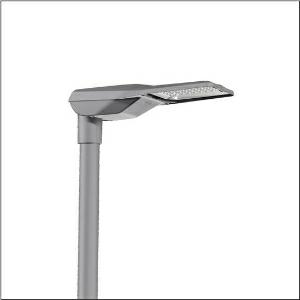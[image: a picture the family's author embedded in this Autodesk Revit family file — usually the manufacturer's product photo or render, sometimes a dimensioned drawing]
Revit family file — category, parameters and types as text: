
# Revit family: streetlight_sl_21_iq_mini___p1_0a_5xe2a31d08hb_09ea
name_source: partatom
category: Lighting Fixtures
units: mm (PartAtom-declared; Revit-internal decimal feet)

## family parameters
Cut with Voids When Loaded = No
Host = Face
Light Source = No
Part Type = Normal
Room Calculation Point = No
Round Connector Dimension = Use Diameter
Shared = No

## types (1)
- --- (1 x LED, 9450 lm, 70.9 W, 3000K)
    Apparent Load = 71 VA
    CIE Flux Codes = 21 50 90 100 100
    Color Rendering = 70
    Color Temperature = 3000K
    Default Elevation = 1800 mm
    Description = Streetlight SL 21 iQ mini, mast luminaire, primary light control with lens, of PMMA, primary optical cover: cover, of toughened safety glass, transparent, light distribution: P1.0a, light emission: direct distribution, primary light characteristic: asymmetric, installation type: post-top, side-entry, LED, High Power LED, rated luminous flux: 9.450lm, luminous efficacy: 133lm/W, light colour: 730, colour temperature: 3000K, control gear: iQ-Comfort, control: Auto-Match, Temp-Guard, Lumen-Switch, Night-Set, Smart-Wire, Light-Fading, Desk-Remote (wireless, voltage-free reading and setting of iQ features in the workshop via application-optimized NFC function/RFID function), optimised constant luminous flux control (CLO 2.0), pre-setting: linear dimming characteristic, mains connection: 220..240V, AC, 50/60Hz, start of lifetime: 71W, end of service life: 75W, reduction: 31W, luminaire housing, of diecast aluminium, powder-coated, SITECO metallic grey (DB 702S), corrosivity category C5 high according to DIN EN ISO 12944, please order mast flange separately, inclination adjustable: 0°, 5°, 10°, 15°, sealing non-destructively replaceable, multi-level sealing system, length: 628mm, width: 235mm, height: 110mm, mast flange for spigot size: 42mm (side-entry): 5XC10008XM4, 60/48mm (side-entry/post-top): 5XC10108XM2, 76/60mm (side-entry/post-top): 5XC10108XM1, mounting height: 4..8m, protection rating (complete): IP66, insulation class (complete): insulation class II (safety insulation), certification: CE, ENEC, ENEC+, VDE, impact resistance: IK10, permissible operating ambient temperature for outdoor applications: -40..+50°C, standard-compliant lighting for roads and squares, packaging unit: 1 piece

Light Distribution: P1.0a
    Height = 110 mm
    Lamp = 1 x LED
    Lamp Light Flux = 9450 lm
    Lamp Power = 70.9 W
    Lamp count = 1
    Length = 625 mm
    Luminous efficacy = 133 lm/W
    Manufacturer = Siteco
    ModVariant = No
    Model = 5XE2A31D08HB
    Number of Poles = 1
    OnlyDefault = Yes
    Power Factor = 1
    Product Name = Streetlight SL 21 iQ mini | P1.0a
    Product group = mast luminaire | pylon top
    ProductGroupID = 6100
    Protection Class = Protection class II
    Protection Degree = IP 66
    RLX_Detail_Level = 1
    RLX_Emergency_Light_Flux = 0 lm
    RLX_Emergency_Type = 0
    RLX_Emergency_Type_DB = No
    RlxData = <blob elided: 37557 chars, md5=27b9ef67>
    Socket = socket
    Standby Power = 0 W
    System Light Flux = 9450 lm
    System Power = 71 W
    Type Comments = factory setting: luminous flux: 100 % | dim-lin: 254 | 711 mA
    Type Image = l_1003519.jpg
    URL = http://relux.com
    VarID = @adj_157185
    Voltage = 0 V
    Weight = 0.00 kg
    Width = 234 mm

## geometry (parser evidence)
native form markers: Blend x4, Sweep x11
no freeform markers — native parametric forms only
